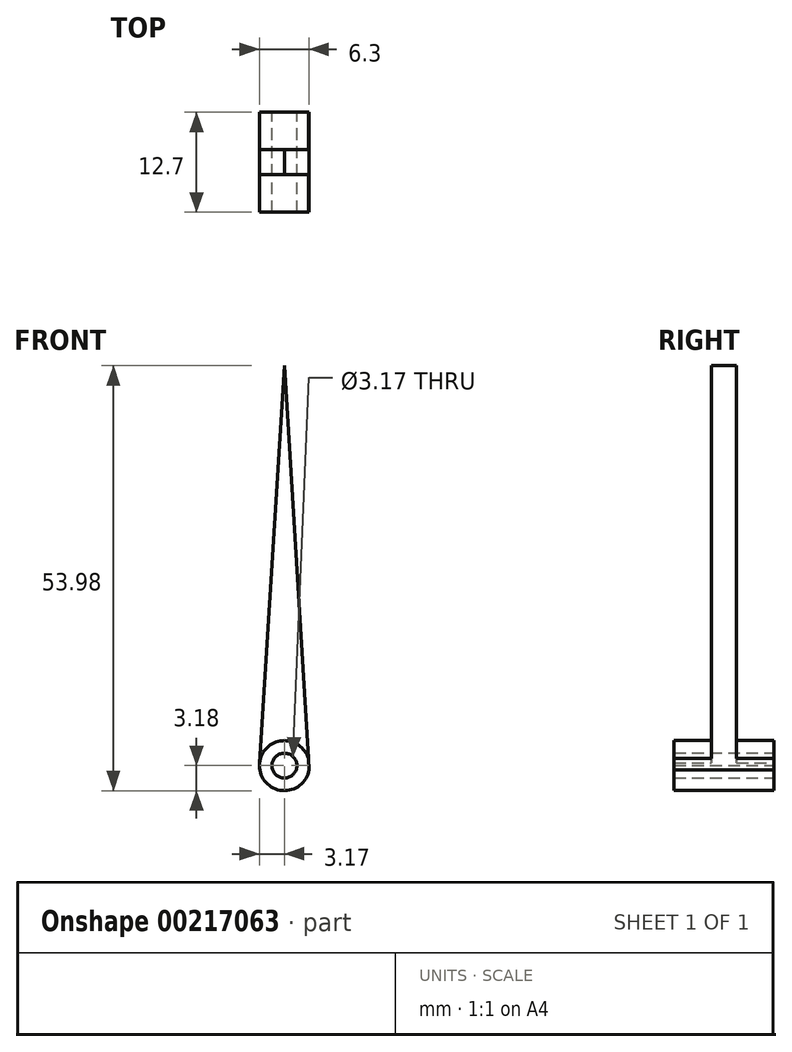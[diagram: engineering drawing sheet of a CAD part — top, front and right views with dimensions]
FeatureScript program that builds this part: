
annotation { "Feature Type Name" : "Feature", "Feature Type Description" : "" }
export const myFeature = defineFeature(function(context is Context, id is Id, definition is map)
    precondition{}
    {
        {
            var Q0;
            Q0=qCreatedBy(makeId("Front.planeOp"),FACE);
            var sketch = newSketch(context, id + "F0", { "sketchPlane" : qUnion([Q0])});
            skCircle(sketch, "E0", {"center": v(0, 0) * mm, "radius": 1.59 * mm});
            skCircle(sketch, "E1", {"center": v(0, 0) * mm, "radius": 3.18 * mm});
            skLineSegment(sketch, "E2", {"start": v(0, 0) * mm, "end": v(0, 3.18) * mm, "construction": true});
            skLineSegment(sketch, "E3", {"start": v(-3.17, 0.1) * mm, "end": v(-3.18, 0) * mm});
            skLineSegment(sketch, "E4", {"start": v(3.18, 0) * mm, "end": v(3.17, 0.19) * mm});
            skLineSegment(sketch, "E5", {"start": v(-3.18, 0) * mm, "end": v(0, 50.8) * mm});
            skLineSegment(sketch, "E6", {"start": v(0, 50.8) * mm, "end": v(3.13, -0.52) * mm});
            skSolve(sketch);
        }
        {
            var Q0;
            Q0=makeQuery(id+"F0.imprint","IMPRINT",FACE,{"disambiguationData":[TD([[makeQuery(id+"F0.imprint","IMPRINT",EDGE,{"derivedFrom":sQuery(id+"F0.wireOp",EDGE,"E0")}),-1.0]])]});
            extrude(context, id + "F1", {"entities" : qUnion([Q0]), "depth" : 12.7 * mm, "symmetric" : true});
        }
        {
            var Q0;
            {var subQ0=sQuery(id+"F0.wireOp",EDGE,"E6");var subQ1=sQuery(id+"F0.wireOp",EDGE,"E1");var subQ2=makeQuery(id+"F0.imprint","INTERSECT",VERTEX,{"disambiguationData":[OD(1.0)],"derivedFrom":[subQ1,subQ0]});Q0=makeQuery(id+"F0.imprint","IMPRINT",FACE,{"disambiguationData":[TD([[makeQuery(id+"F0.imprint","IMPRINT",EDGE,{"disambiguationData":[TD([[subQ2,-1.0]])],"derivedFrom":subQ1}),-1.0]])]});}
            extrude(context, id + "F2", {"entities" : qUnion([Q0]), "operationType" : NewBodyOperationType.ADD, "depth" : 3.17 * mm, "symmetric" : true});
        }
    });
